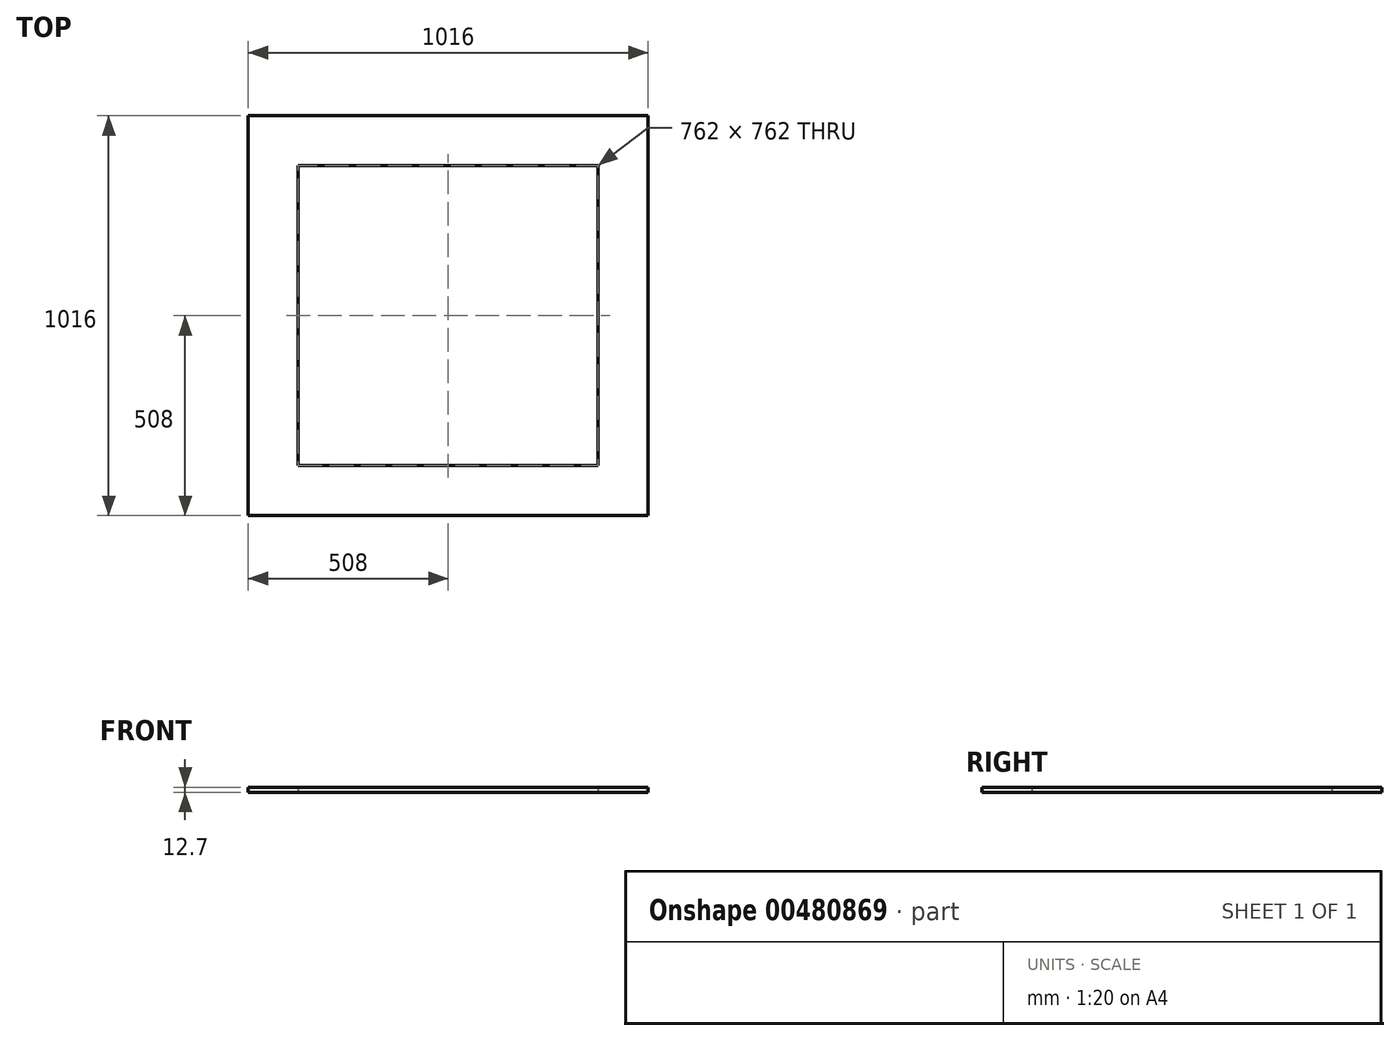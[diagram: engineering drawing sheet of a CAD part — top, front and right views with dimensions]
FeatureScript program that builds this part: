
annotation { "Feature Type Name" : "Feature", "Feature Type Description" : "" }
export const myFeature = defineFeature(function(context is Context, id is Id, definition is map)
    precondition{}
    {
        {
            var Q0;
            Q0=qCreatedBy(makeId("Top.planeOp"),FACE);
            var sketch = newSketch(context, id + "F0", { "sketchPlane" : qUnion([Q0])});
            skLineSegment(sketch, "E0.bottom", {"start": v(508, -508) * mm, "end": v(-508, -508) * mm});
            skLineSegment(sketch, "E0.top", {"start": v(508, 508) * mm, "end": v(-508, 508) * mm});
            skLineSegment(sketch, "E0.left", {"start": v(508, -508) * mm, "end": v(508, 508) * mm});
            skLineSegment(sketch, "E0.right", {"start": v(-508, -508) * mm, "end": v(-508, 508) * mm});
            skPoint(sketch, "E0.middle", {"position": v(0, 0) * mm});
            skLineSegment(sketch, "E1.bottom", {"start": v(381, -381) * mm, "end": v(-381, -381) * mm});
            skLineSegment(sketch, "E1.top", {"start": v(381, 381) * mm, "end": v(-381, 381) * mm});
            skLineSegment(sketch, "E1.left", {"start": v(381, -381) * mm, "end": v(381, 381) * mm});
            skLineSegment(sketch, "E1.right", {"start": v(-381, -381) * mm, "end": v(-381, 381) * mm});
            skSolve(sketch);
        }
        {
            var Q0;
            Q0=makeQuery(id+"F0.imprint","IMPRINT",FACE,{"disambiguationData":[TD([[makeQuery(id+"F0.imprint","IMPRINT",EDGE,{"derivedFrom":sQuery(id+"F0.wireOp",EDGE,"E0.bottom")}),-1.0]])]});
            extrude(context, id + "F1", {"entities" : qUnion([Q0]), "depth" : 12.7 * mm});
        }
    });
